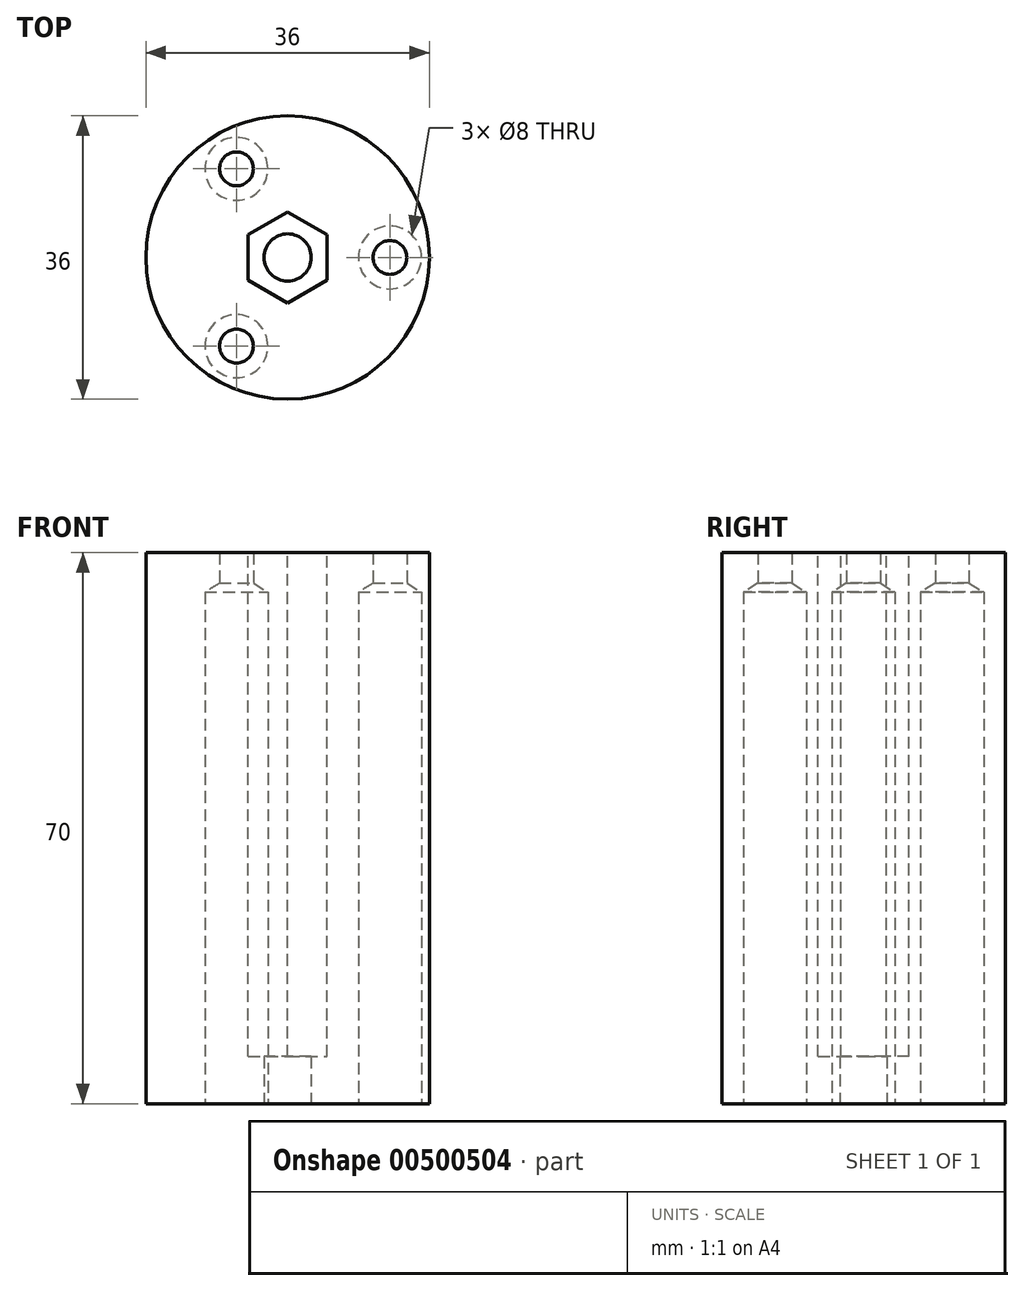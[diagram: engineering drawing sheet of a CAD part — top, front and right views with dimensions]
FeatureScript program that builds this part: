
annotation { "Feature Type Name" : "Feature", "Feature Type Description" : "" }
export const myFeature = defineFeature(function(context is Context, id is Id, definition is map)
    precondition{}
    {
        {
            var Q0;
            Q0=qCreatedBy(makeId("Top.planeOp"),FACE);
            var sketch = newSketch(context, id + "F0", { "sketchPlane" : qUnion([Q0])});
            skCircle(sketch, "E0", {"center": v(0, 0) * mm, "radius": 18 * mm});
            skCircle(sketch, "E1", {"center": v(0, 0) * mm, "radius": 3 * mm});
            skPoint(sketch, "E2", {"position": v(13, 0) * mm});
            skPoint(sketch, "E3.1.0", {"position": v(-6.5, 11.26) * mm});
            skPoint(sketch, "E3.2.0", {"position": v(-6.5, -11.26) * mm});
            skSolve(sketch);
        }
        {
            var Q0;
            Q0=makeQuery(id+"F0.imprint","IMPRINT",FACE,{"disambiguationData":[TD([[makeQuery(id+"F0.imprint","IMPRINT",EDGE,{"derivedFrom":sQuery(id+"F0.wireOp",EDGE,"E0")}),1.0]])]});
            extrude(context, id + "F1", {"entities" : qUnion([Q0]), "depth" : 70 * mm});
        }
        {
            var Q0;
            Q0=makeQuery(id+"F1.opExtrude","CAP_FACE",FACE,{"disambiguationData":[OSD([sQuery(id+"F0.wireOp",EDGE,"E0"),sQuery(id+"F0.wireOp",EDGE,"E1")])],"isStart":false});
            var sketch = newSketch(context, id + "F2", { "sketchPlane" : qUnion([Q0])});
            skPoint(sketch, "E4.center", {"position": v(0, 0) * mm});
            skCircle(sketch, "E5.cCircle", {"center": v(0, 0) * mm, "radius": 5 * mm, "construction": true});
            skLineSegment(sketch, "E5.0", {"start": v(5, 2.89) * mm, "end": v(5, -2.89) * mm});
            skLineSegment(sketch, "E5.1", {"start": v(5, -2.89) * mm, "end": v(0, -5.77) * mm});
            skLineSegment(sketch, "E5.2", {"start": v(0, -5.77) * mm, "end": v(-5, -2.89) * mm});
            skLineSegment(sketch, "E5.3", {"start": v(-5, -2.89) * mm, "end": v(-5, 2.89) * mm});
            skLineSegment(sketch, "E5.4", {"start": v(-5, 2.89) * mm, "end": v(0, 5.77) * mm});
            skLineSegment(sketch, "E5.5", {"start": v(0, 5.77) * mm, "end": v(5, 2.89) * mm});
            skPoint(sketch, "E5.0.midPoint", {"position": v(5, 0) * mm});
            skSolve(sketch);
        }
        {
            var Q0;
            Q0=makeQuery(id+"F2.imprint","IMPRINT",FACE,{"disambiguationData":[TD([[makeQuery(id+"F2.imprint","IMPRINT",EDGE,{"derivedFrom":sQuery(id+"F2.wireOp",EDGE,"E5.0")}),-1.0]])]});
            extrude(context, id + "F3", {"entities" : qUnion([Q0]), "operationType" : NewBodyOperationType.REMOVE, "oppositeDirection" : true, "depth" : 64 * mm});
        }
        {
            var Q0;
            Q0=sQuery(id+"F0.wireOp",VERTEX,"E2");
            var Q1;
            Q1=sQuery(id+"F0.wireOp",VERTEX,"E3.1.0");
            var Q2;
            Q2=sQuery(id+"F0.wireOp",VERTEX,"E3.2.0");
            var Q3;
            Q3=makeQuery(id+"F1.opExtrude","SWEPT_BODY",BODY,{"disambiguationData":[OSD([sQuery(id+"F0.wireOp",EDGE,"E0"),sQuery(id+"F0.wireOp",EDGE,"E1")])]});
            hole(context, id + "F4", {"style" : HoleStyle.SIMPLE, "endStyle" : HoleEndStyle.THROUGH, "oppositeDirection" : true, "holeDiameter" : 4.3 * mm, "isTappedThrough" : true, "tappedDepth" : 12 * mm, "tapClearance" : 3, "locations" : qUnion([Q0, Q1, Q2]), "scope" : qUnion([Q3])});
        }
        {
            var Q0;
            Q0=sQuery(id+"F0.wireOp",VERTEX,"E2");
            var Q1;
            Q1=sQuery(id+"F0.wireOp",VERTEX,"E3.1.0");
            var Q2;
            Q2=sQuery(id+"F0.wireOp",VERTEX,"E3.2.0");
            var Q3;
            Q3=makeQuery(id+"F1.opExtrude","SWEPT_BODY",BODY,{"disambiguationData":[OSD([sQuery(id+"F0.wireOp",EDGE,"E0"),sQuery(id+"F0.wireOp",EDGE,"E1")])]});
            hole(context, id + "F5", {"style" : HoleStyle.SIMPLE, "endStyle" : HoleEndStyle.BLIND, "oppositeDirection" : true, "holeDiameter" : 8 * mm, "holeDepth" : 65 * mm, "isTappedThrough" : true, "tappedDepth" : 12 * mm, "tapClearance" : 3, "locations" : qUnion([Q0, Q1, Q2]), "scope" : qUnion([Q3])});
        }
    });
